# Revit family: ROSENBERG_R_G
name_source: partatom
category: Wyposażenie mechaniczne
revit_build: Autodesk Revit 2017 (Build: 20160225_1515(x64)
units: mm (PartAtom-declared; Revit-internal decimal feet)

## family parameters
Numer OmniClass = 23.75.00.00
Oparty na płaszczyźnie roboczej = Nie
Punkt obliczania pomieszczeń = Nie
Tnij formami wycięć po wczytaniu = Nie
Typ części = Dzieli na
Tytuł OmniClass = Climate Control (HVAC)
Współdzielony = Tak
Wymiar okrągłego złącza = Użyj średnicy
Zawsze pionowo = Tak

## types (9) — shared parameters
Box_Height = 87 mm  [stored 0.285433 ft]
Current = 1 A
Date = 10.2018
Frequence = 50 Hz
Materiał = <Wg kategorii>
Opis = Tube Fan
Producent = Rosenberg
URL = https://www.rosenberg.pl
Version = 1
Voltage = 230 V

## per-type parameters (varying)
| type | Air_flow | Box_Width | Collar_Length | Diameter_connector | F1 | Hole_Diameter | Power | Pressure | Protection_Class | Total_Length | Weight | Width_Diameter | b1 |
| 100 G.3BK | 200.0 m³/h | 43 mm | 25 mm  [stored 0.082021 ft] | 100 mm  [stored 0.328084 ft] | 151 mm | 95 mm  [stored 0.31168 ft] | 104 W | 467.0 Pa | IP44 | 226 mm | 3.30 kg | 243 mm | 57 mm |
| 125 G.3BK | 204.0 m³/h | 41 mm | 25 mm  [stored 0.082021 ft] | 125 mm | 153 mm | 120 mm  [stored 0.393701 ft] | 90 W | 470.0 Pa | IP44 | 230 mm | 3.50 kg | 243 mm | 58 mm |
| 160 G.3BK | 416.0 m³/h | 41 mm | 25 mm  [stored 0.082021 ft] | 160 mm | 135 mm | 155 mm  [stored 0.50853 ft] | 130 W | 446.0 Pa | IP44 | 202 mm | 3.70 kg | 341 mm | 51 mm |
| 200 G.3BK | 542.0 m³/h | 41 mm | 25 mm  [stored 0.082021 ft] | 200 mm  [stored 0.656168 ft] | 170 mm | 195 mm | 160 W | 424.0 Pa | IP44 | 255 mm | 3.90 kg | 341 mm | 64 mm |
| 250 G.3BK | 592.0 m³/h | 41 mm | 30 mm  [stored 0.0984252 ft] | 250 mm  [stored 0.82021 ft] | 171 mm | 245 mm  [stored 0.803806 ft] | 160 W | 388.0 Pa | IP44 | 256 mm | 3.90 kg | 341 mm | 64 mm |
| 315 G.3DI | 772.0 m³/h | 41 mm | 30 mm  [stored 0.0984252 ft] | 315 mm  [stored 1.03346 ft] | 170 mm | 310 mm  [stored 1.01706 ft] | 180 W | 407.0 Pa | IP54 | 255 mm | 6.50 kg | 402 mm | 64 mm |
| 315L G.3DI | 1029.0 m³/h | 41 mm | 30 mm  [stored 0.0984252 ft] | 315 mm  [stored 1.03346 ft] | 170 mm | 310 mm  [stored 1.01706 ft] | 320 W | 549.0 Pa | IP54 | 255 mm | 6.50 kg | 402 mm | 64 mm |
| 355 G.3DI | 1391.0 m³/h | 41 mm | 35 mm  [stored 0.114829 ft] | 355 mm  [stored 1.1647 ft] | 267 mm | 350 mm  [stored 1.14829 ft] | 240 W | 296.0 Pa | IP54 | 400 mm  [stored 1.31234 ft] | 11.30 kg | 490 mm  [stored 1.60761 ft] | 100 mm  [stored 0.328084 ft] |
| 355L G.3DI | 1317.0 m³/h | 41 mm | 35 mm  [stored 0.114829 ft] | 355 mm  [stored 1.1647 ft] | 267 mm | 350 mm  [stored 1.14829 ft] | 320 W | 414.0 Pa | IP54 | 400 mm  [stored 1.31234 ft] | 11.30 kg | 490 mm  [stored 1.60761 ft] | 100 mm  [stored 0.328084 ft] |

note: column(s) folded — value = type name in every type: Model

note: [stored X ft] marks values corroborated as IEEE doubles in the binary element streams (Revit-internal decimal feet)

## geometry (parser evidence)
native form markers: Blend x4, Sweep x5
no freeform markers — native parametric forms only
